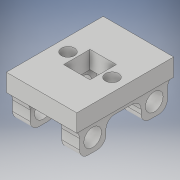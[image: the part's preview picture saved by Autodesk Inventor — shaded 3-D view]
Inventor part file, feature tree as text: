
AUTODESK INVENTOR PART (.ipt)
format: ipt  version: 2019 (Build 230136000, 136)  size: 230,912 bytes
history: native  units: mm
features: sketch x6, extrude x5, fillet x4, hole x1
ambient origin geometry x8: Origin, YZ Plane, XZ Plane, XY Plane, X Axis, Y Axis, Z Axis, Center Point
bodies: Solid1 (feature_tree)
feature tree (16):
  extrude  "Extrusion1"  Depth=80.0mm
  extrude  "Extrusion2"  Depth=30.0mm
  hole  "Hole1"  [1 undecoded]
  extrude  "Extrusion3"  Depth=20.0mm
  fillet  "Fillet1"  Radius=2.0mm
  fillet  "Fillet3"  Radius=30.0mm
  fillet  "Fillet4"  Radius=15.0mm
  extrude  "Extrusion4"  Depth=25.0mm
  extrude  "Extrusion5"  Depth=25.0mm
  fillet  "Fillet5"  Radius=15.0mm
  sketch  "Sketch1"  dims[d0=110.0mm d1=80.0mm]
  sketch  "Sketch2"  dims[d2=20.0mm d3=0.0mm d4=30.0mm]
  sketch  "Sketch3"  dims[d5=20.0mm d6=20.0mm]
  sketch  "Sketch4"  dims[d7=2.0mm d8=20.0mm d9=2.0mm d10=30.0mm d11=0.0mm]
  sketch  "Sketch5"  dims[d12=20.0mm d13=6.0mm d14=4.0mm d15=2.0mm d16=90.0deg d17=15.0mm d18=20.594885mm d19=15.0mm]
  sketch  "Sketch6"  dims[d20=15.0mm d21=25.0mm d23=25.0mm d24=15.0mm d25=0.0mm d26=10.0mm d28=10.0mm d29=10.0mm d30=30.0mm d31=30.0mm d32=20.0mm d33=0.0mm d34=5.0mm d35=0.0mm d36=10.0mm d22=0.75mm]
note: 1 required parameter value undecoded (feature->parameter linkage not recoverable at this tier; creation-order binding heuristic only, values carry confidence <= 0.55)
